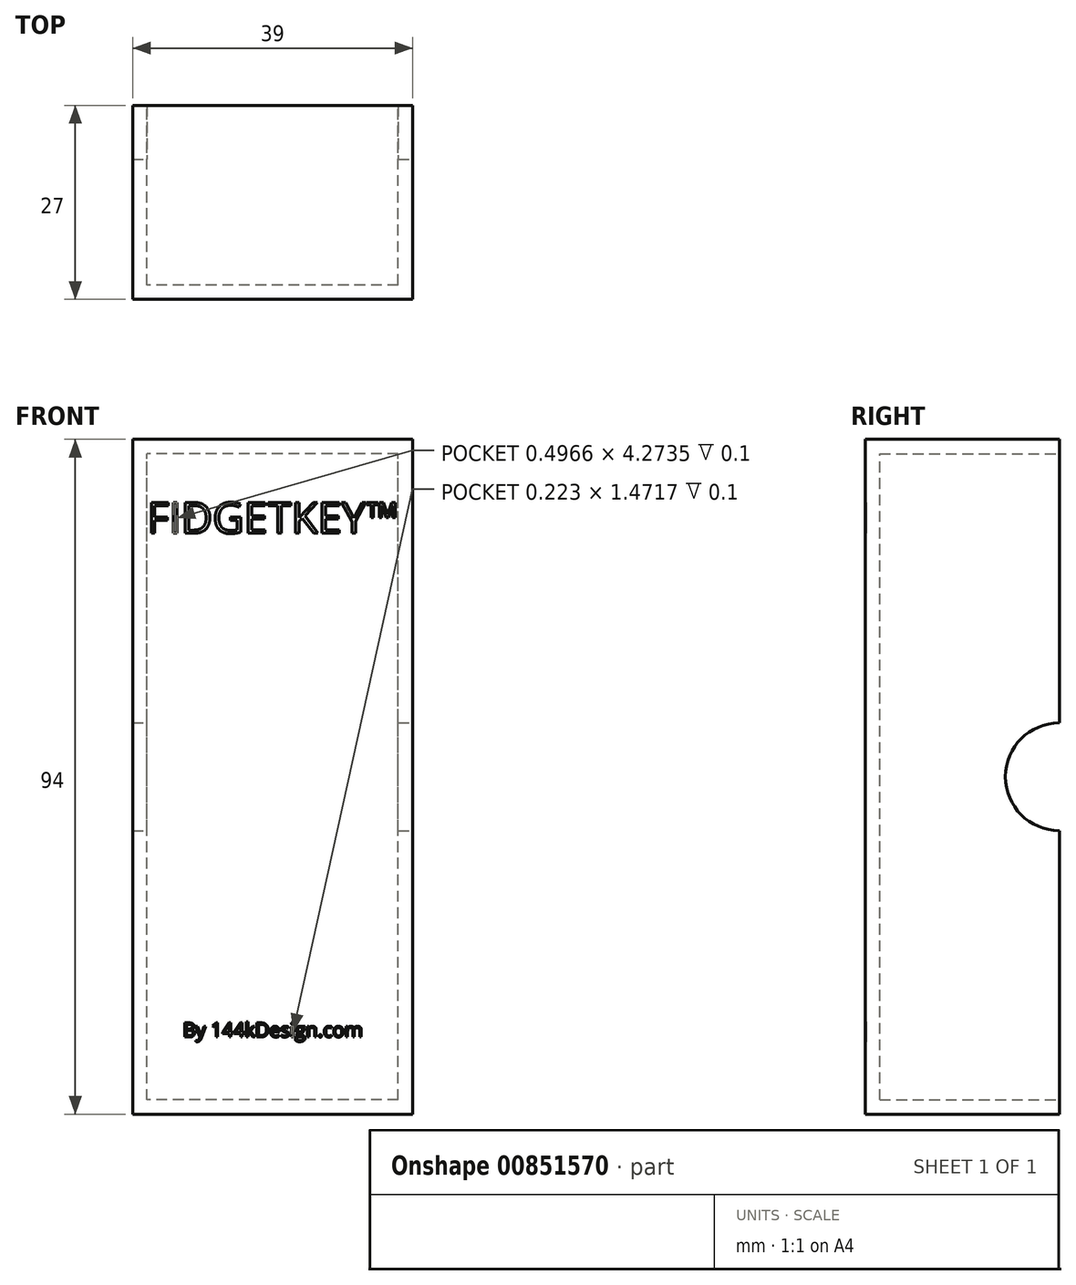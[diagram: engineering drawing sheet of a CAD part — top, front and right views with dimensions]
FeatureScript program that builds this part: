
annotation { "Feature Type Name" : "Feature", "Feature Type Description" : "" }
export const myFeature = defineFeature(function(context is Context, id is Id, definition is map)
    precondition{}
    {
        {
            var Q0;
            Q0=qCreatedBy(makeId("Front.planeOp"),FACE);
            var sketch = newSketch(context, id + "F0", { "sketchPlane" : qUnion([Q0])});
            skLineSegment(sketch, "E0.bottom", {"start": v(19.5, -47) * mm, "end": v(-19.5, -47) * mm});
            skLineSegment(sketch, "E0.top", {"start": v(19.5, 47) * mm, "end": v(-19.5, 47) * mm});
            skLineSegment(sketch, "E0.left", {"start": v(19.5, -47) * mm, "end": v(19.5, 47) * mm});
            skLineSegment(sketch, "E0.right", {"start": v(-19.5, -47) * mm, "end": v(-19.5, 47) * mm});
            skPoint(sketch, "E0.middle", {"position": v(0, 0) * mm});
            skSolve(sketch);
        }
        {
            var Q0;
            Q0 = qSketchRegion(id + "F0", true);
            extrude(context, id + "F1", {"entities" : qUnion([Q0]), "depth" : 27 * mm, "offsetDistance" : 25 * mm});
        }
        {
            var Q0;
            Q0=makeQuery(id+"F1.opExtrude","CAP_FACE",FACE,{"disambiguationData":[OSD([sQuery(id+"F0.wireOp",EDGE,"E0.bottom"),sQuery(id+"F0.wireOp",EDGE,"E0.top"),sQuery(id+"F0.wireOp",EDGE,"E0.left"),sQuery(id+"F0.wireOp",EDGE,"E0.right")])],"isStart":true});
            shell(context, id + "F2", {"entities" : qUnion([Q0]), "thickness" : 2 * mm});
        }
        {
            var Q0;
            Q0=qCreatedBy(makeId("Right.planeOp"),FACE);
            var sketch = newSketch(context, id + "F3", { "sketchPlane" : qUnion([Q0])});
            skCircle(sketch, "E1", {"center": v(0, 0) * mm, "radius": 7.5 * mm});
            skSolve(sketch);
        }
        {
            var Q0;
            Q0 = qSketchRegion(id + "F3", true);
            extrude(context, id + "F4", {"entities" : qUnion([Q0]), "operationType" : NewBodyOperationType.REMOVE, "endBound" : BoundingType.SYMMETRIC, "oppositeDirection" : true, "depth" : 50 * mm, "offsetDistance" : 25 * mm});
        }
        {
            var Q0;
            Q0=makeQuery(id+"F1.opExtrude","CAP_FACE",FACE,{"disambiguationData":[OSD([sQuery(id+"F0.wireOp",EDGE,"E0.bottom"),sQuery(id+"F0.wireOp",EDGE,"E0.top"),sQuery(id+"F0.wireOp",EDGE,"E0.left"),sQuery(id+"F0.wireOp",EDGE,"E0.right")])],"isStart":false});
            var sketch = newSketch(context, id + "F5", { "sketchPlane" : qUnion([Q0])});
            skText(sketch, "E2", { "text": "FIDGETKEY™", "fontName": "OpenSans-Regular.ttf"});
            const initialGuessF5  = {"E2": [-0.0175, 0.03392, 1, 0, 0.00431]};
            skSetInitialGuess(sketch, initialGuessF5);
            skSolve(sketch);
        }
        {
            var Q0;
            Q0=makeQuery(id+"F5.imprint","IMPRINT",FACE,{"disambiguationData":[TD([[makeQuery(id+"F5.imprint","IMPRINT",EDGE,{"derivedFrom":sQuery(id+"F5.wireOp",EDGE,"E2.sketch_text.stroke-0")}),1.0]])]});
            var sketch = newSketch(context, id + "F6", { "sketchPlane" : qUnion([Q0])});
            skText(sketch, "E3", { "text": "By 144kDesign.com", "fontName": "OpenSans-Regular.ttf"});
            const initialGuessF6  = {"E3": [-0.0125, -0.03625, 1, 0, 0.00198]};
            skSetInitialGuess(sketch, initialGuessF6);
            skSolve(sketch);
        }
        {
            var Q0;
            Q0 = qSketchRegion(id + "F5", true);
            extrude(context, id + "F7", {"entities" : qUnion([Q0]), "operationType" : NewBodyOperationType.REMOVE, "oppositeDirection" : true, "depth" : 0.1 * mm, "offsetDistance" : 25 * mm});
        }
        {
            var Q0;
            Q0 = qSketchRegion(id + "F6", true);
            extrude(context, id + "F8", {"entities" : qUnion([Q0]), "operationType" : NewBodyOperationType.REMOVE, "surfaceOperationType" : NewSurfaceOperationType.ADD, "oppositeDirection" : true, "depth" : 0.1 * mm, "offsetDistance" : 25 * mm});
        }
    });
